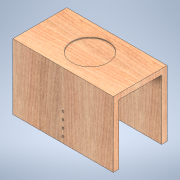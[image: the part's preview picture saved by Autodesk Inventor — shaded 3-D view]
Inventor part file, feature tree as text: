
AUTODESK INVENTOR PART (.ipt)
format: ipt  version: 2022.2 (Build 262287000, 287)  size: 174,080 bytes
history: native  units: in
note: dims shown in document units (in); Inventor stores cm internally (conversion verified against a paired STEP export)
features: sketch x4, extrude x3, mirror x1, hole x1, pattern_linear x1
ambient origin geometry x8: Origin, YZ Plane, XZ Plane, XY Plane, X Axis, Y Axis, Z Axis, Center Point
bodies: Solid1 (feature_tree)
feature tree (10):
  extrude  "Extrusion1"  Depth=0.75in TaperAngle=0.0deg
  extrude  "Extrusion2"  Depth=9.0in
  mirror  "Mirror1"
  hole  "Hole1"  [1 undecoded]
  pattern_linear  "Rectangular Pattern1"  Count1=4 Spacing1=1.0in
  extrude  "Extrusion3"  Depth=0.1in
  sketch  "Sketch1"  dims[d0=5.875in d1=0.75in d2=0.0in]
  sketch  "Sketch3"  dims[d4=13.75in d5=9.0in]
  sketch  "Sketch4"  dims[d6=0.75in d7=0.0in]
  sketch  "Sketch5"  dims[d8=0.266in d9=0.75in d10=0.507in d11=0.25in d12=0.5635in d13=1.0in d14=0.8108in d15=1.5748in d17=1.0in d18=5.0in d19=0.1in d20=0.0in]
note: 1 required parameter value undecoded (feature->parameter linkage not recoverable at this tier; creation-order binding heuristic only, values carry confidence <= 0.55)
